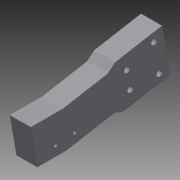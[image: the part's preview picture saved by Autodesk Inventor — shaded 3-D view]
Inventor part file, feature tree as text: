
AUTODESK INVENTOR PART (.ipt)
format: ipt  version: 2013 (Build 170138000, 138)  size: 184,832 bytes
history: native  units: mm
features: sketch x6, hole x4, extrude x3, other x2, pattern_circular x1
ambient origin geometry x8: Origin, YZ Plane, XZ Plane, XY Plane, X Axis, Y Axis, Z Axis, Center Point
feature tree (16):
  other  "ソリッド1"
  extrude  "押し出し1"  Depth=20.0mm
  hole  "穴2"  [1 undecoded]
  extrude  "押し出し2"  Depth=10.0mm
  hole  "穴3"  [1 undecoded]
  hole  "穴4"  [1 undecoded]
  pattern_circular  "円形状パターン3"  [2 undecoded]
  hole  "穴5"  [1 undecoded]
  extrude  "押し出し3"  Depth=4.0mm
  sketch  "スケッチ4"
  sketch  "スケッチ5"
  sketch  "スケッチ6"
  sketch  "スケッチ7"
  sketch  "スケッチ8"
  sketch  "スケッチ9"
  other  "断面エッジを投影1"
note: 6 required parameter values undecoded (feature->parameter linkage not recoverable at this tier; creation-order binding heuristic only, values carry confidence <= 0.55)
